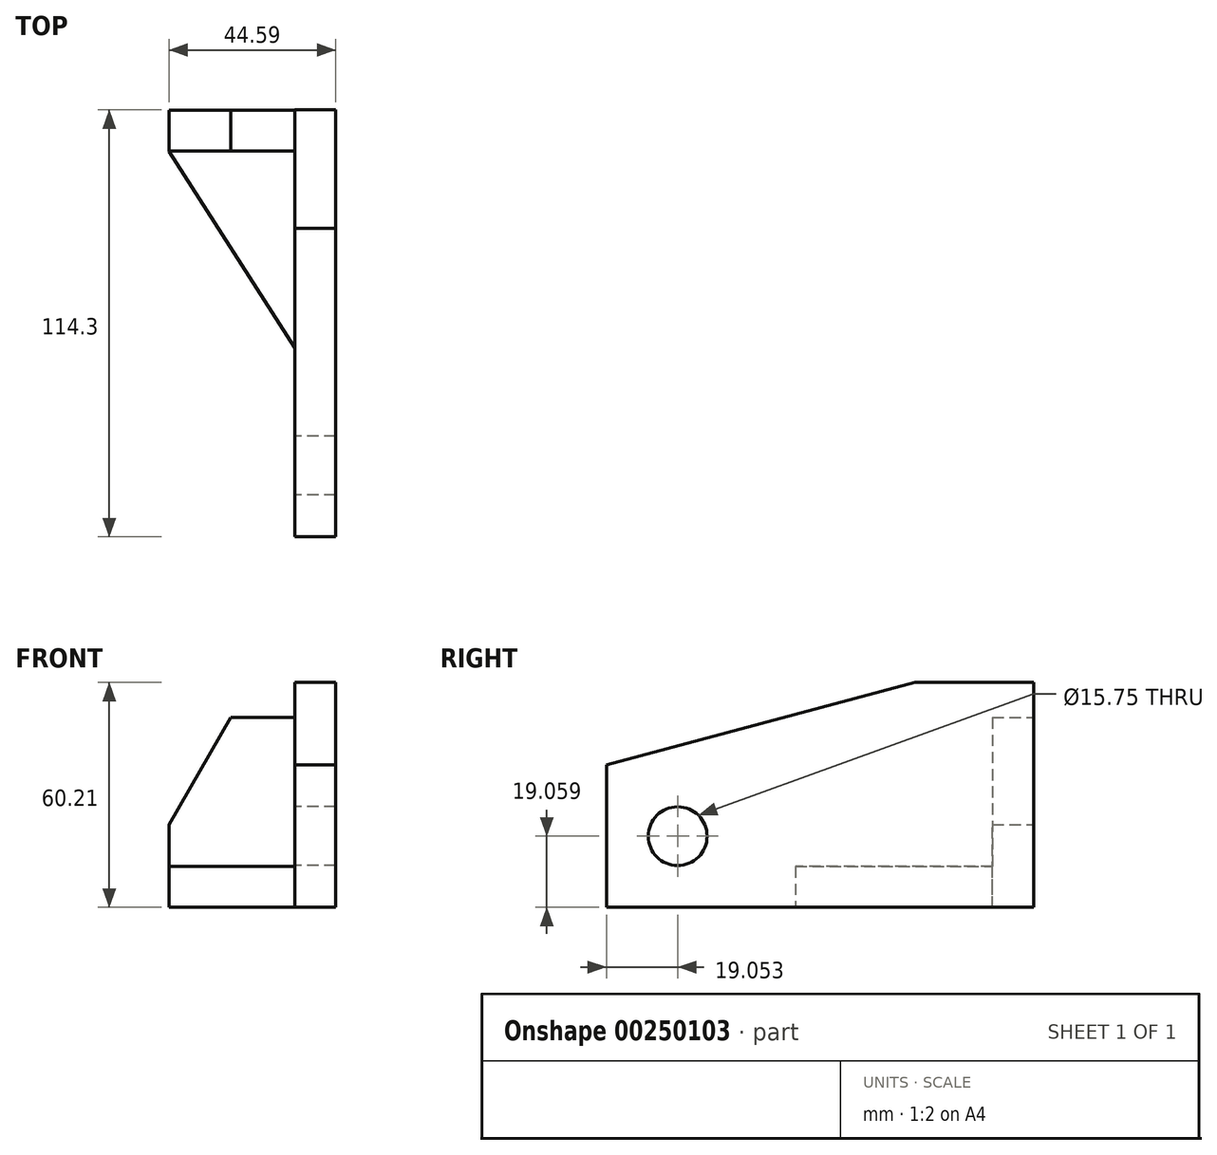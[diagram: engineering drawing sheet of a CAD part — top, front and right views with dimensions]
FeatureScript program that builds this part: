
annotation { "Feature Type Name" : "Feature", "Feature Type Description" : "" }
export const myFeature = defineFeature(function(context is Context, id is Id, definition is map)
    precondition{}
    {
        {
            var Q0;
            Q0=qCreatedBy(makeId("Right.planeOp"),FACE);
            var sketch = newSketch(context, id + "F0", { "sketchPlane" : qUnion([Q0])});
            skLineSegment(sketch, "E0.bottom", {"start": v(-31.64, 60.2) * mm, "end": v(0.11, 60.2) * mm});
            skLineSegment(sketch, "E0.top", {"start": v(-114.19, 0) * mm, "end": v(0.11, 0) * mm});
            skLineSegment(sketch, "E0.left", {"start": v(-114.19, 38.09) * mm, "end": v(-114.19, 0) * mm});
            skLineSegment(sketch, "E0.right", {"start": v(0.11, 60.2) * mm, "end": v(0.11, 0) * mm});
            skLineSegment(sketch, "E1", {"start": v(-114.19, 38.09) * mm, "end": v(-31.64, 60.2) * mm});
            skCircle(sketch, "E2", {"center": v(-95.14, 19.06) * mm, "radius": 7.87 * mm});
            skLineSegment(sketch, "E3", {"start": v(-114.19, 0) * mm, "end": v(-95.14, 0) * mm, "construction": true});
            skLineSegment(sketch, "E4", {"start": v(-95.14, 19.06) * mm, "end": v(-95.14, 0) * mm, "construction": true});
            skSolve(sketch);
        }
        {
            var Q0;
            Q0 = qSketchRegion(id + "F0", true);
            extrude(context, id + "F1", {"entities" : qUnion([Q0]), "depth" : 10.92 * mm});
        }
        {
            var Q0;
            Q0=qCreatedBy(makeId("Top.planeOp"),FACE);
            var sketch = newSketch(context, id + "F2", { "sketchPlane" : qUnion([Q0])});
            skLineSegment(sketch, "E5.bottom", {"start": v(0, -63.63) * mm, "end": v(10.85, -63.63) * mm});
            skLineSegment(sketch, "E5.top", {"start": v(-33.6, -0.13) * mm, "end": v(10.85, -0.13) * mm});
            skLineSegment(sketch, "E5.left", {"start": v(-33.6, -11.05) * mm, "end": v(-33.6, -0.13) * mm});
            skLineSegment(sketch, "E5.right", {"start": v(10.85, -63.63) * mm, "end": v(10.85, -0.13) * mm});
            skLineSegment(sketch, "E6", {"start": v(0, -63.63) * mm, "end": v(-33.6, -11.05) * mm});
            skSolve(sketch);
        }
        {
            var Q0;
            Q0 = qSketchRegion(id + "F2", true);
            extrude(context, id + "F3", {"entities" : qUnion([Q0]), "operationType" : NewBodyOperationType.ADD, "depth" : 10.92 * mm});
        }
        {
            var Q0;
            Q0=qCreatedBy(makeId("Front.planeOp"),FACE);
            var sketch = newSketch(context, id + "F4", { "sketchPlane" : qUnion([Q0])});
            skLineSegment(sketch, "E7.bottom", {"start": v(10.78, 0) * mm, "end": v(-33.67, 0) * mm});
            skLineSegment(sketch, "E7.top", {"start": v(10.78, 50.8) * mm, "end": v(-17.1, 50.8) * mm});
            skLineSegment(sketch, "E7.left", {"start": v(10.78, 0) * mm, "end": v(10.78, 50.8) * mm});
            skLineSegment(sketch, "E7.right", {"start": v(-33.67, 0) * mm, "end": v(-33.67, 22.1) * mm});
            skLineSegment(sketch, "E8", {"start": v(-17.1, 50.8) * mm, "end": v(-33.67, 22.1) * mm});
            skSolve(sketch);
        }
        {
            var Q0;
            Q0 = qSketchRegion(id + "F4", true);
            extrude(context, id + "F5", {"entities" : qUnion([Q0]), "operationType" : NewBodyOperationType.ADD, "depth" : 10.92 * mm});
        }
    });
